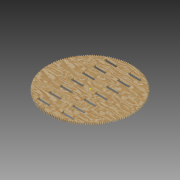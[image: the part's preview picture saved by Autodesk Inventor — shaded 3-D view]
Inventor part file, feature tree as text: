
AUTODESK INVENTOR PART (.ipt)
format: ipt  version: 2020 (Build 240168000, 168)  size: 1,143,808 bytes
history: native  units: mm
features: sketch x6, extrude x3, plane x3, pattern_linear x2, mirror x2, other x1, loft x1
ambient origin geometry x8: Origin, YZ Plane, XZ Plane, XY Plane, X Axis, Y Axis, Z Axis, Center Point
bodies: Body1 (feature_tree)
feature tree (18):
  extrude  "Extrusion8"  Depth=940.0mm
  sketch  "Sketch4"  dims[d5=100.0mm d6=950.0mm]
  other  "Spur Gear2"
  extrude  "Extrusion9"  Depth=950.0mm
  plane  "Work Plane1"
  loft  "Loft1"
  pattern_linear  "Rectangular Pattern1"  Count1=12  [1 undecoded]
  pattern_linear  "Rectangular Pattern2"  Count1=84  [1 undecoded]
  plane  "Work Plane2"
  mirror  "Mirror1"
  plane  "Work Plane3"
  mirror  "Mirror2"
  extrude  "Extrusion11"  Depth=13.0mm
  sketch  "Sketch1"  dims[d0=1050.0mm d1=940.0mm]
  sketch  "Sketch5"  dims[d12=200.0mm d13=100.0mm d15=109.0mm d16=30.0mm d17=30.0mm d18=15.0mm d19=15.0mm]
  sketch  "Sketch7"  dims[d25=15.0mm d29=120.0mm]
  sketch  "Sketch8"  dims[d33=30.0mm d36=30.0mm d37=188.0mm d38=15.0mm d40=188.0mm d41=188.0mm d42=30.0mm d46=640.0mm d47=320.0mm d50=920.0mm d51=880.0mm d52=190.0mm]
  sketch  "Sketch9"  dims[d53=95.0mm d67=840.0mm d69=240.0mm d75=26.0mm d82=19.05mm d83=0.0mm d84=210.0mm d85=210.0mm d86=8.0mm d87=8.0mm d88=8.0mm d89=8.0mm d90=8.0mm d91=8.0mm d92=74.0mm d94=32.0mm d95=16.0mm d96=135.0mm d97=135.0mm d98=135.0mm d99=135.0mm d100=135.0mm d101=135.0mm d102=140.0mm d103=0.0mm d104=4.0mm d105=2.0mm d106=2.0mm d107=2.0mm d108=2.0mm d109=2.0mm d110=2.0mm d111=2.0mm d112=2.0mm d113=2.0mm d114=2.0mm d115=2.0mm d116=2.0mm d117=2.0mm d118=2.0mm d119=2.0mm d120=2.0mm d121=2.0mm d122=2.0mm d123=2.0mm d124=2.0mm d125=2.0mm d126=0.0mm d127=0.0mm d130=-6.2mm d131=17.0mm d132=0.0mm d133=90.0deg d134=0.0mm d135=90.0deg d136=20.0mm d138=154.58mm d139=20.0mm d141=364.585mm d142=50.8mm d143=13.0mm d144=0.0mm]
note: 2 required parameter values undecoded (feature->parameter linkage not recoverable at this tier; creation-order binding heuristic only, values carry confidence <= 0.55)
